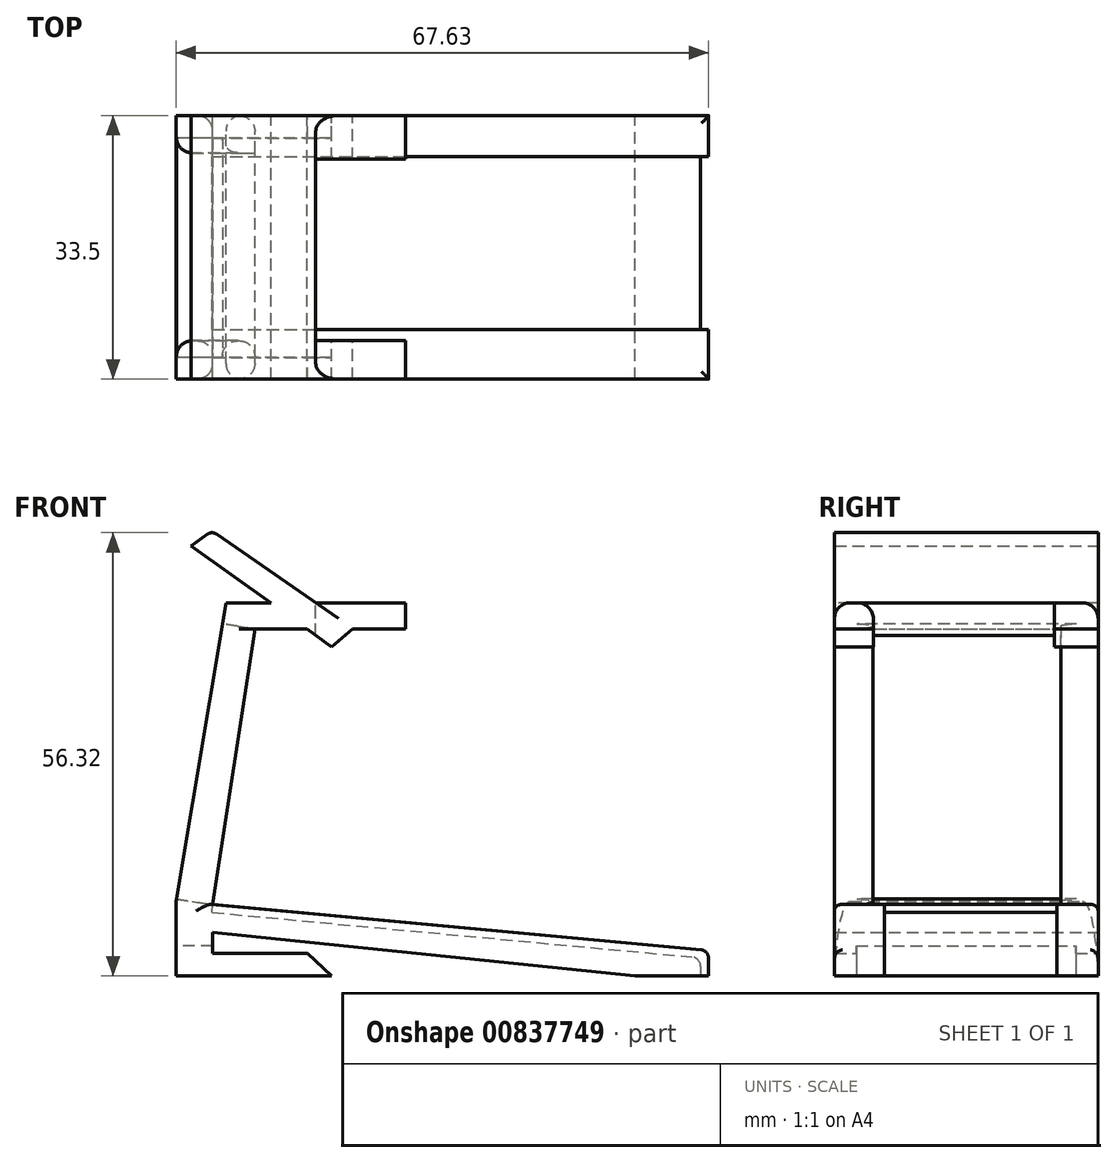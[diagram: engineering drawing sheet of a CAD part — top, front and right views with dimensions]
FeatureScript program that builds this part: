
annotation { "Feature Type Name" : "Feature", "Feature Type Description" : "" }
export const myFeature = defineFeature(function(context is Context, id is Id, definition is map)
    precondition{}
    {
        {
            var Q0;
            Q0=qCreatedBy(makeId("Front.planeOp"),FACE);
            var sketch = newSketch(context, id + "F0", { "sketchPlane" : qUnion([Q0])});
            skLineSegment(sketch, "E0", {"start": v(-46.01, -14.62) * mm, "end": v(-34, -14.62) * mm});
            skLineSegment(sketch, "E1", {"start": v(-34, -14.62) * mm, "end": v(-30.94, -17.5) * mm});
            skLineSegment(sketch, "E2", {"start": v(-30.94, -17.5) * mm, "end": v(-50.68, -17.5) * mm});
            skLineSegment(sketch, "E3", {"start": v(-50.68, -17.5) * mm, "end": v(-50.68, -7.98) * mm});
            skLineSegment(sketch, "E4", {"start": v(-46.01, -8.42) * mm, "end": v(16.95, -14.26) * mm});
            skLineSegment(sketch, "E5", {"start": v(16.95, -14.26) * mm, "end": v(16.95, -17.5) * mm});
            skLineSegment(sketch, "E6", {"start": v(16.95, -17.5) * mm, "end": v(7.62, -17.5) * mm});
            skLineSegment(sketch, "E7", {"start": v(-46.01, -14.62) * mm, "end": v(-46.01, -11.93) * mm});
            skLineSegment(sketch, "E8", {"start": v(-46.01, -11.93) * mm, "end": v(7.62, -17.5) * mm});
            skLineSegment(sketch, "E9", {"start": v(-50.68, -7.98) * mm, "end": v(-44.35, 29.92) * mm});
            skLineSegment(sketch, "E10", {"start": v(-44.35, 29.92) * mm, "end": v(-38.64, 29.92) * mm});
            skLineSegment(sketch, "E11", {"start": v(-21.52, 29.92) * mm, "end": v(-21.52, 26.62) * mm});
            skLineSegment(sketch, "E12", {"start": v(-21.52, 26.62) * mm, "end": v(-28.24, 26.62) * mm});
            skLineSegment(sketch, "E13", {"start": v(-40.67, 26.62) * mm, "end": v(-46.01, -8.42) * mm});
            skLineSegment(sketch, "E14", {"start": v(-32.93, 29.92) * mm, "end": v(-46.12, 39.05) * mm});
            skLineSegment(sketch, "E15", {"start": v(-46.12, 39.05) * mm, "end": v(-48.79, 37.15) * mm});
            skLineSegment(sketch, "E16", {"start": v(-48.79, 37.15) * mm, "end": v(-38.64, 29.92) * mm});
            skLineSegment(sketch, "E17", {"start": v(-34.07, 26.62) * mm, "end": v(-30.9, 24.34) * mm});
            skLineSegment(sketch, "E18", {"start": v(-30.9, 24.34) * mm, "end": v(-28.24, 26.62) * mm});
            skLineSegment(sketch, "E19.trimOffspring", {"start": v(-32.93, 29.92) * mm, "end": v(-21.52, 29.92) * mm});
            skLineSegment(sketch, "E20.trimOffspring", {"start": v(-34.07, 26.62) * mm, "end": v(-40.67, 26.62) * mm});
            skSolve(sketch);
        }
        {
            var Q0;
            Q0 = qSketchRegion(id + "F0", true);
            extrude(context, id + "F1", {"entities" : qUnion([Q0]), "depth" : 33.5 * mm, "offsetDistance" : 25 * mm});
        }
        {
            var Q0;
            Q0=makeQuery(id+"F1.opExtrude","SWEPT_FACE",FACE,{"disambiguationData":[OSD([sQuery(id+"F0.wireOp",EDGE,"E13")])]});
            var sketch = newSketch(context, id + "F2", { "sketchPlane" : qUnion([Q0])});
            skLineSegment(sketch, "E21.bottom", {"start": v(-28.62, -15.26) * mm, "end": v(-4.75, -15.26) * mm});
            skLineSegment(sketch, "E21.top", {"start": v(-28.62, 20.18) * mm, "end": v(-4.75, 20.18) * mm});
            skLineSegment(sketch, "E21.left", {"start": v(-28.62, -15.26) * mm, "end": v(-28.62, 20.18) * mm});
            skLineSegment(sketch, "E21.right", {"start": v(-4.75, -15.26) * mm, "end": v(-4.75, 20.18) * mm});
            skSolve(sketch);
        }
        {
            var Q0;
            Q0 = qSketchRegion(id + "F2", true);
            extrude(context, id + "F3", {"entities" : qUnion([Q0]), "operationType" : NewBodyOperationType.REMOVE, "oppositeDirection" : true, "depth" : 25 * mm, "offsetDistance" : 25 * mm});
        }
        {
            var Q0;
            Q0=makeQuery(id+"F1.opExtrude","SWEPT_FACE",FACE,{"disambiguationData":[OSD([sQuery(id+"F0.wireOp",EDGE,"E19.trimOffspring")])]});
            var sketch = newSketch(context, id + "F4", { "sketchPlane" : qUnion([Q0])});
            skLineSegment(sketch, "E22.bottom", {"start": v(-21.52, -28.56) * mm, "end": v(-32.93, -28.56) * mm});
            skLineSegment(sketch, "E22.top", {"start": v(-21.52, -5.56) * mm, "end": v(-32.93, -5.56) * mm});
            skLineSegment(sketch, "E22.left", {"start": v(-21.52, -28.56) * mm, "end": v(-21.52, -5.56) * mm});
            skLineSegment(sketch, "E22.right", {"start": v(-32.93, -28.56) * mm, "end": v(-32.93, -5.56) * mm});
            skSolve(sketch);
        }
        {
            var Q0;
            Q0 = qSketchRegion(id + "F4", true);
            extrude(context, id + "F5", {"entities" : qUnion([Q0]), "operationType" : NewBodyOperationType.REMOVE, "oppositeDirection" : true, "depth" : 25 * mm, "offsetDistance" : 25 * mm});
        }
        {
            var Q0;
            Q0=makeQuery(id+"F1.opExtrude","CAP_EDGE",EDGE,{"disambiguationData":[OSD([sQuery(id+"F0.wireOp",EDGE,"E9")])],"isStart":true});
            var Q1;
            Q1=makeQuery(id+"F1.opExtrude","CAP_EDGE",EDGE,{"disambiguationData":[OSD([sQuery(id+"F0.wireOp",EDGE,"E13")])],"isStart":true});
            var Q2;
            Q2=makeQuery(id+"F3.boolean.opBoolean","COPY",EDGE,{"derivedFrom":makeQuery(id+"F3.opExtrude","CAP_EDGE",EDGE,{"disambiguationData":[OSD([sQuery(id+"F2.wireOp",EDGE,"E21.right")])],"isStart":true})});
            var Q3;
            Q3=makeQuery(id+"F3.boolean.opBoolean","INTERSECT",EDGE,{"derivedFrom":[makeQuery(id+"F1.opExtrude","SWEPT_FACE",FACE,{"disambiguationData":[OSD([sQuery(id+"F0.wireOp",EDGE,"E9")])]}),makeQuery(id+"F3.opExtrude","SWEPT_FACE",FACE,{"disambiguationData":[OSD([sQuery(id+"F2.wireOp",EDGE,"E21.right")])]})]});
            var Q4;
            Q4=makeQuery(id+"F3.boolean.opBoolean","INTERSECT",EDGE,{"derivedFrom":[makeQuery(id+"F1.opExtrude","SWEPT_FACE",FACE,{"disambiguationData":[OSD([sQuery(id+"F0.wireOp",EDGE,"E9")])]}),makeQuery(id+"F3.opExtrude","SWEPT_FACE",FACE,{"disambiguationData":[OSD([sQuery(id+"F2.wireOp",EDGE,"E21.left")])]})]});
            var Q5;
            Q5=makeQuery(id+"F3.boolean.opBoolean","COPY",EDGE,{"derivedFrom":makeQuery(id+"F3.opExtrude","CAP_EDGE",EDGE,{"disambiguationData":[OSD([sQuery(id+"F2.wireOp",EDGE,"E21.left")])],"isStart":true})});
            var Q6;
            Q6=makeQuery(id+"F1.opExtrude","CAP_EDGE",EDGE,{"disambiguationData":[OSD([sQuery(id+"F0.wireOp",EDGE,"E9")])],"isStart":false});
            var Q7;
            Q7=makeQuery(id+"F1.opExtrude","CAP_EDGE",EDGE,{"disambiguationData":[OSD([sQuery(id+"F0.wireOp",EDGE,"E13")])],"isStart":false});
            var Q8;
            Q8=makeQuery(id+"F1.opExtrude","CAP_EDGE",EDGE,{"disambiguationData":[OSD([sQuery(id+"F0.wireOp",EDGE,"E19.trimOffspring")])],"isStart":false});
            var Q9;
            Q9=makeQuery(id+"F5.boolean.opBoolean","COPY",EDGE,{"derivedFrom":makeQuery(id+"F5.opExtrude","CAP_EDGE",EDGE,{"disambiguationData":[OSD([sQuery(id+"F4.wireOp",EDGE,"E22.bottom")])],"isStart":true})});
            var Q10;
            Q10=makeQuery(id+"F5.boolean.opBoolean","COPY",EDGE,{"derivedFrom":makeQuery(id+"F5.opExtrude","CAP_EDGE",EDGE,{"disambiguationData":[OSD([sQuery(id+"F4.wireOp",EDGE,"E22.top")])],"isStart":true})});
            var Q11;
            Q11=makeQuery(id+"F1.opExtrude","CAP_EDGE",EDGE,{"disambiguationData":[OSD([sQuery(id+"F0.wireOp",EDGE,"E19.trimOffspring")])],"isStart":true});
            fillet(context, id + "F6", {"entities" : qUnion([Q0, Q1, Q2, Q3, Q4, Q5, Q6, Q7, Q8, Q9, Q10, Q11]), "radius" : 2 * mm, "tangentPropagation" : true, "allowEdgeOverflow" : false});
        }
        {
            var Q0;
            Q0=makeQuery(id+"F1.opExtrude","SWEPT_FACE",FACE,{"disambiguationData":[OSD([sQuery(id+"F0.wireOp",EDGE,"E4")])]});
            var sketch = newSketch(context, id + "F7", { "sketchPlane" : qUnion([Q0])});
            skLineSegment(sketch, "E23.bottom", {"start": v(-45.04, -27.17) * mm, "end": v(18.2, -27.17) * mm});
            skLineSegment(sketch, "E23.top", {"start": v(-45.04, -5.24) * mm, "end": v(18.2, -5.24) * mm});
            skLineSegment(sketch, "E23.left", {"start": v(-45.04, -27.17) * mm, "end": v(-45.04, -5.24) * mm});
            skLineSegment(sketch, "E24.bottom", {"start": v(18.2, -27.17) * mm, "end": v(29.67, -27.17) * mm});
            skLineSegment(sketch, "E24.top", {"start": v(18.2, -5.24) * mm, "end": v(29.67, -5.24) * mm});
            skLineSegment(sketch, "E24.right", {"start": v(29.67, -27.17) * mm, "end": v(29.67, -5.24) * mm});
            skSolve(sketch);
        }
        {
            var Q0;
            Q0 = qSketchRegion(id + "F7", true);
            var Q1;
            {var subQ0=sQuery(id+"F7.wireOp",EDGE,"E23.bottom");Q1=makeQuery(id+"F7.imprint","IMPRINT",FACE,{"disambiguationData":[TD([[makeQuery(id+"F7.imprint","IMPRINT",EDGE,{"derivedFrom":subQ0}),1.0]])]});}
            extrude(context, id + "F8", {"entities" : qUnion([Q0, Q1]), "operationType" : NewBodyOperationType.REMOVE, "oppositeDirection" : true, "depth" : 1 * mm, "offsetDistance" : 25 * mm});
        }
        {
            var Q0;
            Q0=makeQuery(id+"F1.opExtrude","SWEPT_FACE",FACE,{"disambiguationData":[OSD([sQuery(id+"F0.wireOp",EDGE,"E5")])]});
            var sketch = newSketch(context, id + "F9", { "sketchPlane" : qUnion([Q0])});
            skLineSegment(sketch, "E25.bottom", {"start": v(-27.17, -15.27) * mm, "end": v(-5.24, -15.27) * mm});
            skLineSegment(sketch, "E25.top", {"start": v(-27.17, -17.5) * mm, "end": v(-5.24, -17.5) * mm});
            skLineSegment(sketch, "E25.left", {"start": v(-27.17, -15.27) * mm, "end": v(-27.17, -17.5) * mm});
            skLineSegment(sketch, "E25.right", {"start": v(-5.24, -15.27) * mm, "end": v(-5.24, -17.5) * mm});
            skLineSegment(sketch, "E26.top", {"start": v(-27.17, -14.26) * mm, "end": v(-5.24, -14.26) * mm});
            skLineSegment(sketch, "E26.left", {"start": v(-27.17, -15.27) * mm, "end": v(-27.17, -14.26) * mm});
            skLineSegment(sketch, "E26.right", {"start": v(-5.24, -15.27) * mm, "end": v(-5.24, -14.26) * mm});
            skSolve(sketch);
        }
        {
            var Q0;
            Q0 = qSketchRegion(id + "F9", true);
            extrude(context, id + "F10", {"entities" : qUnion([Q0]), "operationType" : NewBodyOperationType.REMOVE, "oppositeDirection" : true, "depth" : 1 * mm, "offsetDistance" : 25 * mm});
        }
        {
            var Q0;
            Q0=makeQuery(id+"F10.boolean.opBoolean","INTERSECT",EDGE,{"derivedFrom":[makeQuery(id+"F8.boolean.opBoolean","COPY",FACE,{"derivedFrom":makeQuery(id+"F8.opExtrude","CAP_FACE",FACE,{"disambiguationData":[OSD([sQuery(id+"F7.wireOp",EDGE,"E23.bottom"),sQuery(id+"F7.wireOp",EDGE,"E23.top"),sQuery(id+"F7.wireOp",EDGE,"E23.left"),sQuery(id+"F7.wireOp",EDGE,"E24.bottom"),sQuery(id+"F7.wireOp",EDGE,"E24.top"),sQuery(id+"F7.wireOp",EDGE,"E24.right")])],"isStart":false})}),makeQuery(id+"F10.opExtrude","CAP_FACE",FACE,{"disambiguationData":[OSD([sQuery(id+"F9.wireOp",EDGE,"E25.top"),sQuery(id+"F9.wireOp",EDGE,"E25.left"),sQuery(id+"F9.wireOp",EDGE,"E25.right"),sQuery(id+"F9.wireOp",EDGE,"E26.top"),sQuery(id+"F9.wireOp",EDGE,"E26.left"),sQuery(id+"F9.wireOp",EDGE,"E26.right")])],"isStart":false})]});
            var Q1;
            Q1=makeQuery(id+"F10.boolean.opBoolean","COPY",EDGE,{"derivedFrom":makeQuery(id+"F10.opExtrude","CAP_EDGE",EDGE,{"disambiguationData":[OSD([sQuery(id+"F9.wireOp",EDGE,"E25.top")])],"isStart":false})});
            fillet(context, id + "F11", {"entities" : qUnion([Q0, Q1]), "radius" : 1.2 * mm, "tangentPropagation" : true, "allowEdgeOverflow" : false});
        }
        {
            var Q0;
            Q0=makeQuery(id+"F1.opExtrude","SWEPT_FACE",FACE,{"disambiguationData":[OSD([sQuery(id+"F0.wireOp",EDGE,"E2")])]});
            var sketch = newSketch(context, id + "F12", { "sketchPlane" : qUnion([Q0])});
            skLineSegment(sketch, "E27.bottom", {"start": v(-30.94, 30.74) * mm, "end": v(-50.68, 30.74) * mm});
            skLineSegment(sketch, "E27.top", {"start": v(-30.94, 2.84) * mm, "end": v(-50.68, 2.84) * mm});
            skLineSegment(sketch, "E27.left", {"start": v(-30.94, 30.74) * mm, "end": v(-30.94, 2.84) * mm});
            skLineSegment(sketch, "E27.right", {"start": v(-50.68, 30.74) * mm, "end": v(-50.68, 2.84) * mm});
            skSolve(sketch);
        }
        {
            var Q0;
            Q0 = qSketchRegion(id + "F12", true);
            extrude(context, id + "F13", {"entities" : qUnion([Q0]), "operationType" : NewBodyOperationType.REMOVE, "oppositeDirection" : true, "depth" : 3.8 * mm, "offsetDistance" : 25 * mm});
        }
        {
            var Q0;
            Q0=makeQuery(id+"F1.opExtrude","CAP_EDGE",EDGE,{"disambiguationData":[OSD([sQuery(id+"F0.wireOp",EDGE,"E4")])],"isStart":true});
            var Q1;
            Q1=makeQuery(id+"F1.opExtrude","CAP_EDGE",EDGE,{"disambiguationData":[OSD([sQuery(id+"F0.wireOp",EDGE,"E4")])],"isStart":false});
            var Q2;
            {var subQ0=sQuery(id+"F0.wireOp",EDGE,"E5");var subQ1=sQuery(id+"F0.wireOp",EDGE,"E4");Q2=makeQuery(id+"F8.boolean.opBoolean","SPLIT",EDGE,{"disambiguationData":[TD([makeQuery(id+"F8.opExtrude","SWEPT_FACE",FACE,{"disambiguationData":[OSD([sQuery(id+"F7.wireOp",EDGE,"E23.top"),sQuery(id+"F7.wireOp",EDGE,"E24.top")])]})])],"derivedFrom":makeQuery(id+"F1.opExtrude","SWEPT_EDGE",EDGE,{"disambiguationData":[OSD([subQ1,subQ0])]})});}
            var Q3;
            {var subQ0=sQuery(id+"F0.wireOp",EDGE,"E5");var subQ1=sQuery(id+"F0.wireOp",EDGE,"E4");Q3=makeQuery(id+"F8.boolean.opBoolean","SPLIT",EDGE,{"disambiguationData":[TD([makeQuery(id+"F8.opExtrude","SWEPT_FACE",FACE,{"disambiguationData":[OSD([sQuery(id+"F7.wireOp",EDGE,"E23.bottom"),sQuery(id+"F7.wireOp",EDGE,"E24.bottom")])]})])],"derivedFrom":makeQuery(id+"F1.opExtrude","SWEPT_EDGE",EDGE,{"disambiguationData":[OSD([subQ1,subQ0])]})});}
            var Q4;
            Q4=makeQuery(id+"F1.opExtrude","SWEPT_EDGE",EDGE,{"disambiguationData":[OSD([sQuery(id+"F0.wireOp",EDGE,"E14"),sQuery(id+"F0.wireOp",EDGE,"E15")])]});
            fillet(context, id + "F14", {"entities" : qUnion([Q0, Q1, Q2, Q3, Q4]), "radius" : 1 * mm, "tangentPropagation" : true, "allowEdgeOverflow" : false});
        }
    });
